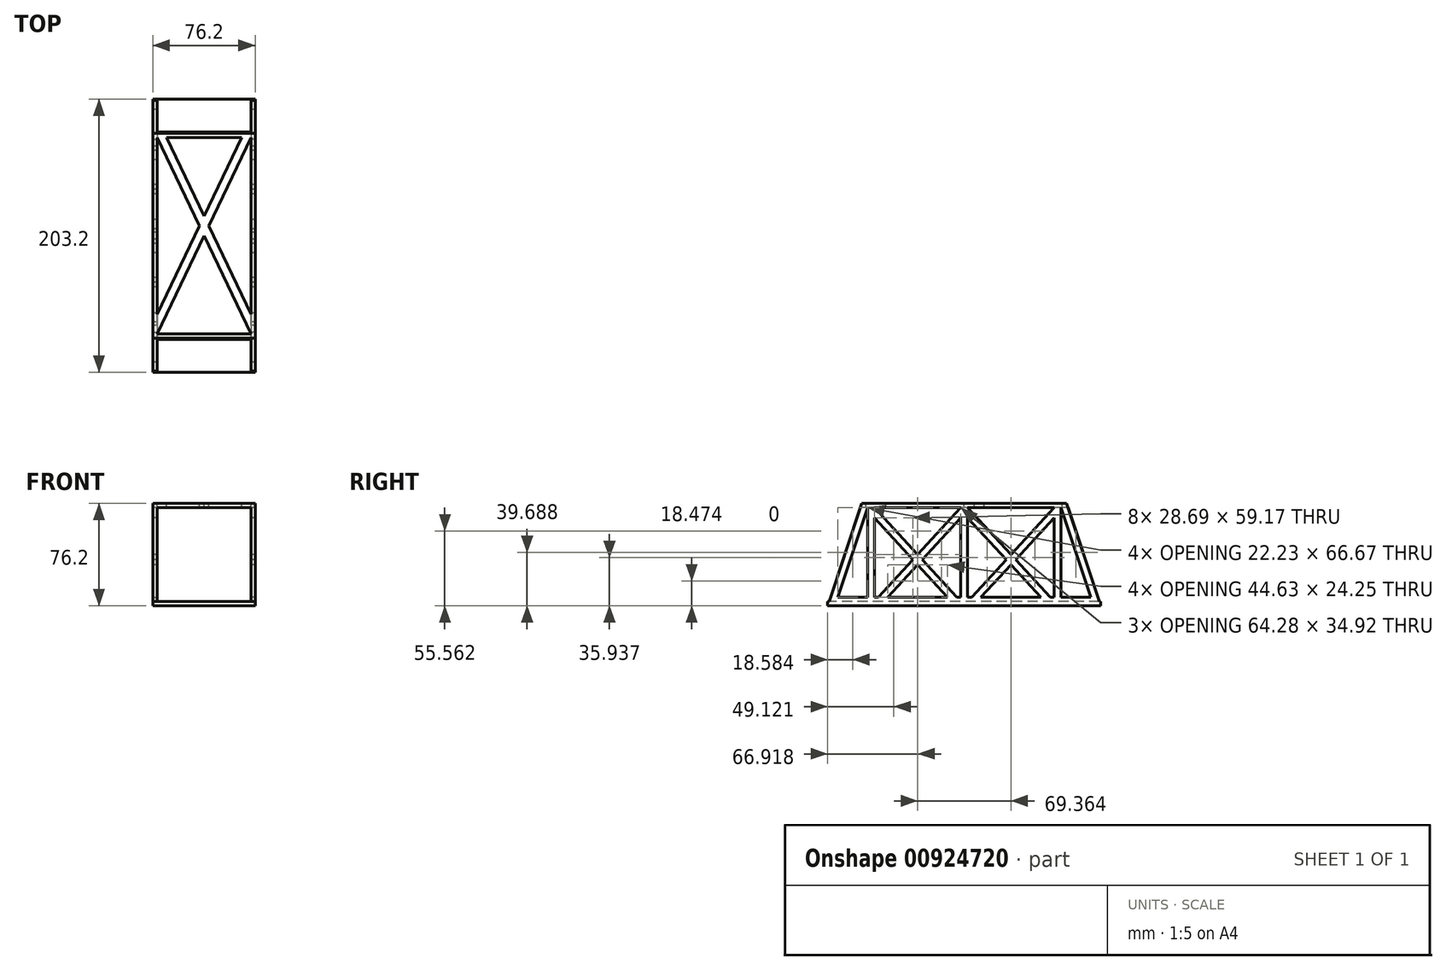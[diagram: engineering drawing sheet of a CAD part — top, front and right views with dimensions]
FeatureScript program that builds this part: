
annotation { "Feature Type Name" : "Feature", "Feature Type Description" : "" }
export const myFeature = defineFeature(function(context is Context, id is Id, definition is map)
    precondition{}
    {
        {
            var Q0;
            Q0=qCreatedBy(makeId("Right.planeOp"),FACE);
            var sketch = newSketch(context, id + "F0", { "sketchPlane" : qUnion([Q0])});
            skLineSegment(sketch, "E0", {"start": v(-101.6, -38.1) * mm, "end": v(101.6, -38.1) * mm});
            skLineSegment(sketch, "E1", {"start": v(101.6, -38.1) * mm, "end": v(76.2, 38.1) * mm});
            skLineSegment(sketch, "E2", {"start": v(76.2, 38.1) * mm, "end": v(-76.2, 38.1) * mm});
            skLineSegment(sketch, "E3", {"start": v(-76.2, 38.1) * mm, "end": v(-101.6, -38.1) * mm});
            skSolve(sketch);
        }
        {
            var Q0;
            Q0=qSketchRegion(id+"F0",true);
            extrude(context, id + "F1", {"entities" : qUnion([Q0]), "endBound" : BoundingType.SYMMETRIC, "depth" : 76.2 * mm, "offsetDistance" : 25.4 * mm});
        }
        {
            var Q0;
            Q0=qCreatedBy(makeId("Front.planeOp"),FACE);
            var sketch = newSketch(context, id + "F2", { "sketchPlane" : qUnion([Q0])});
            skLineSegment(sketch, "E4.bottom", {"start": v(34.92, -34.93) * mm, "end": v(-34.93, -34.93) * mm});
            skLineSegment(sketch, "E4.top", {"start": v(34.92, 34.93) * mm, "end": v(-34.93, 34.92) * mm});
            skLineSegment(sketch, "E4.left", {"start": v(34.92, -34.93) * mm, "end": v(34.92, 34.92) * mm});
            skLineSegment(sketch, "E4.right", {"start": v(-34.93, -34.93) * mm, "end": v(-34.93, 34.92) * mm});
            skPoint(sketch, "E4.middle", {"position": v(0, 0) * mm});
            skSolve(sketch);
        }
        {
            var Q0;
            Q0=qSketchRegion(id+"F2",true);
            extrude(context, id + "F3", {"entities" : qUnion([Q0]), "operationType" : NewBodyOperationType.REMOVE, "endBound" : BoundingType.SYMMETRIC, "oppositeDirection" : true, "depth" : 254 * mm, "offsetDistance" : 25.4 * mm});
        }
        {
            var Q0;
            Q0=makeQuery(id+"F1.opExtrude","CAP_FACE",FACE,{"disambiguationData":[OSD([sQuery(id+"F0.wireOp",EDGE,"E0"),sQuery(id+"F0.wireOp",EDGE,"E1"),sQuery(id+"F0.wireOp",EDGE,"E2"),sQuery(id+"F0.wireOp",EDGE,"E3")])],"isStart":true});
            var sketch = newSketch(context, id + "F4", { "sketchPlane" : qUnion([Q0])});
            skLineSegment(sketch, "E5", {"start": v(-95.19, -34.93) * mm, "end": v(-71.9, 34.93) * mm});
            skLineSegment(sketch, "E6", {"start": v(-71.9, 34.93) * mm, "end": v(-71.9, -34.92) * mm});
            skLineSegment(sketch, "E7", {"start": v(-71.9, -34.92) * mm, "end": v(-95.19, -34.92) * mm});
            skLineSegment(sketch, "E8.MirrorCS", {"start": v(71.9, 34.93) * mm, "end": v(71.9, -34.92) * mm});
            skLineSegment(sketch, "E9.MirrorCS", {"start": v(71.9, -34.92) * mm, "end": v(95.19, -34.92) * mm});
            skLineSegment(sketch, "E10.MirrorCS", {"start": v(95.19, -34.93) * mm, "end": v(71.9, 34.93) * mm});
            skLineSegment(sketch, "E11", {"start": v(-71.9, 34.93) * mm, "end": v(71.9, 34.93) * mm});
            skLineSegment(sketch, "E12", {"start": v(-71.9, -34.92) * mm, "end": v(71.9, -34.92) * mm});
            skLineSegment(sketch, "E13", {"start": v(-66.82, 34.93) * mm, "end": v(-66.82, -34.93) * mm});
            skLineSegment(sketch, "E14", {"start": v(66.82, 34.93) * mm, "end": v(66.82, -34.92) * mm});
            skLineSegment(sketch, "E15.bottom", {"start": v(2.54, -34.93) * mm, "end": v(-2.54, -34.93) * mm});
            skLineSegment(sketch, "E15.top", {"start": v(2.54, 34.93) * mm, "end": v(-2.54, 34.93) * mm});
            skLineSegment(sketch, "E15.left", {"start": v(2.54, -34.93) * mm, "end": v(2.54, 34.93) * mm});
            skLineSegment(sketch, "E15.right", {"start": v(-2.54, -34.93) * mm, "end": v(-2.54, 34.93) * mm});
            skPoint(sketch, "E15.middle", {"position": v(0, 0) * mm});
            skLineSegment(sketch, "E16", {"start": v(-66.82, 34.93) * mm, "end": v(-2.54, -34.93) * mm});
            skLineSegment(sketch, "E17", {"start": v(66.82, 34.93) * mm, "end": v(2.54, -34.93) * mm});
            skLineSegment(sketch, "E18", {"start": v(-66.82, 27.42) * mm, "end": v(-9.44, -34.93) * mm});
            skLineSegment(sketch, "E19", {"start": v(66.82, 27.42) * mm, "end": v(9.44, -34.93) * mm});
            skLineSegment(sketch, "E20", {"start": v(-2.54, 34.93) * mm, "end": v(-66.82, -34.93) * mm});
            skLineSegment(sketch, "E21", {"start": v(-2.54, 27.42) * mm, "end": v(-59.92, -34.93) * mm});
            skLineSegment(sketch, "E22.MirrorCS", {"start": v(2.54, 34.93) * mm, "end": v(66.82, -34.93) * mm});
            skLineSegment(sketch, "E23.MirrorCS", {"start": v(2.54, 27.42) * mm, "end": v(59.92, -34.93) * mm});
            skSolve(sketch);
        }
        {
            var Q0;
            Q0=makeQuery(id+"F4.imprint","IMPRINT",FACE,{"disambiguationData":[TD([[makeQuery(id+"F4.imprint","IMPRINT",EDGE,{"derivedFrom":sQuery(id+"F4.wireOp",EDGE,"E5")}),-1.0]])]});
            var Q1;
            {var subQ1=sQuery(id+"F4.wireOp",EDGE,"E13");var subQ3=sQuery(id+"F4.wireOp",EDGE,"E18");var subQ4=makeQuery(id+"F4.imprint","INTERSECT",VERTEX,{"derivedFrom":[subQ1,subQ3]});Q1=makeQuery(id+"F4.imprint","IMPRINT",FACE,{"disambiguationData":[TD([[makeQuery(id+"F4.imprint","IMPRINT",EDGE,{"disambiguationData":[TD([[subQ4,-1.0]])],"derivedFrom":subQ3}),-1.0]])]});}
            var Q2;
            {var subQ0=sQuery(id+"F4.wireOp",EDGE,"E16");var subQ3=sQuery(id+"F4.wireOp",EDGE,"E20");var subQ5=makeQuery(id+"F4.imprint","INTERSECT",VERTEX,{"derivedFrom":[subQ0,subQ3]});Q2=makeQuery(id+"F4.imprint","IMPRINT",FACE,{"disambiguationData":[TD([[makeQuery(id+"F4.imprint","IMPRINT",EDGE,{"disambiguationData":[TD([[subQ5,1.0]])],"derivedFrom":subQ0}),1.0]])]});}
            var Q3;
            {var subQ1=sQuery(id+"F4.wireOp",EDGE,"E15.right");var subQ3=sQuery(id+"F4.wireOp",EDGE,"E21");var subQ4=makeQuery(id+"F4.imprint","INTERSECT",VERTEX,{"derivedFrom":[subQ1,subQ3]});Q3=makeQuery(id+"F4.imprint","IMPRINT",FACE,{"disambiguationData":[TD([[makeQuery(id+"F4.imprint","IMPRINT",EDGE,{"disambiguationData":[TD([[subQ4,-1.0]])],"derivedFrom":subQ3}),1.0]])]});}
            var Q4;
            {var subQ0=sQuery(id+"F4.wireOp",EDGE,"E18");var subQ1=sQuery(id+"F4.wireOp",EDGE,"E12");var subQ2=makeQuery(id+"F4.imprint","INTERSECT",VERTEX,{"derivedFrom":[subQ1,subQ0]});Q4=makeQuery(id+"F4.imprint","IMPRINT",FACE,{"disambiguationData":[TD([[makeQuery(id+"F4.imprint","IMPRINT",EDGE,{"disambiguationData":[TD([[subQ2,1.0]])],"derivedFrom":subQ1}),1.0]])]});}
            var Q5;
            {var subQ1=sQuery(id+"F4.wireOp",EDGE,"E15.left");var subQ3=sQuery(id+"F4.wireOp",EDGE,"E23.MirrorCS");var subQ4=makeQuery(id+"F4.imprint","INTERSECT",VERTEX,{"derivedFrom":[subQ1,subQ3]});Q5=makeQuery(id+"F4.imprint","IMPRINT",FACE,{"disambiguationData":[TD([[makeQuery(id+"F4.imprint","IMPRINT",EDGE,{"disambiguationData":[TD([[subQ4,-1.0]])],"derivedFrom":subQ3}),-1.0]])]});}
            var Q6;
            {var subQ0=sQuery(id+"F4.wireOp",EDGE,"E17");var subQ3=sQuery(id+"F4.wireOp",EDGE,"E22.MirrorCS");var subQ5=makeQuery(id+"F4.imprint","INTERSECT",VERTEX,{"derivedFrom":[subQ0,subQ3]});Q6=makeQuery(id+"F4.imprint","IMPRINT",FACE,{"disambiguationData":[TD([[makeQuery(id+"F4.imprint","IMPRINT",EDGE,{"disambiguationData":[TD([[subQ5,1.0]])],"derivedFrom":subQ0}),-1.0]])]});}
            var Q7;
            {var subQ1=sQuery(id+"F4.wireOp",EDGE,"E14");var subQ3=sQuery(id+"F4.wireOp",EDGE,"E19");var subQ4=makeQuery(id+"F4.imprint","INTERSECT",VERTEX,{"derivedFrom":[subQ1,subQ3]});Q7=makeQuery(id+"F4.imprint","IMPRINT",FACE,{"disambiguationData":[TD([[makeQuery(id+"F4.imprint","IMPRINT",EDGE,{"disambiguationData":[TD([[subQ4,-1.0]])],"derivedFrom":subQ3}),1.0]])]});}
            var Q8;
            {var subQ0=sQuery(id+"F4.wireOp",EDGE,"E19");var subQ1=sQuery(id+"F4.wireOp",EDGE,"E12");var subQ2=makeQuery(id+"F4.imprint","INTERSECT",VERTEX,{"derivedFrom":[subQ1,subQ0]});Q8=makeQuery(id+"F4.imprint","IMPRINT",FACE,{"disambiguationData":[TD([[makeQuery(id+"F4.imprint","IMPRINT",EDGE,{"disambiguationData":[TD([[subQ2,-1.0]])],"derivedFrom":subQ1}),1.0]])]});}
            var Q9;
            Q9=makeQuery(id+"F4.imprint","IMPRINT",FACE,{"disambiguationData":[TD([[makeQuery(id+"F4.imprint","IMPRINT",EDGE,{"derivedFrom":sQuery(id+"F4.wireOp",EDGE,"E8.MirrorCS")}),1.0]])]});
            extrude(context, id + "F5", {"entities" : qUnion([Q0, Q1, Q2, Q3, Q4, Q5, Q6, Q7, Q8, Q9]), "operationType" : NewBodyOperationType.REMOVE, "oppositeDirection" : true, "depth" : 76.2 * mm, "offsetDistance" : 25.4 * mm});
        }
        {
            var Q0;
            Q0=makeQuery(id+"F1.opExtrude","SWEPT_FACE",FACE,{"disambiguationData":[OSD([sQuery(id+"F0.wireOp",EDGE,"E2")])]});
            var sketch = newSketch(context, id + "F6", { "sketchPlane" : qUnion([Q0])});
            skLineSegment(sketch, "E24.bottom", {"start": v(34.92, -73.03) * mm, "end": v(-34.93, -73.03) * mm});
            skLineSegment(sketch, "E24.top", {"start": v(34.92, 73.03) * mm, "end": v(-34.92, 73.03) * mm});
            skLineSegment(sketch, "E24.left", {"start": v(34.92, -73.03) * mm, "end": v(34.93, 73.02) * mm});
            skLineSegment(sketch, "E24.right", {"start": v(-34.93, -73.03) * mm, "end": v(-34.92, 73.02) * mm});
            skPoint(sketch, "E24.middle", {"position": v(0, 0) * mm});
            skLineSegment(sketch, "E25", {"start": v(-34.92, 73.03) * mm, "end": v(34.92, -73.03) * mm});
            skLineSegment(sketch, "E26", {"start": v(34.92, 73.03) * mm, "end": v(-34.92, -73.03) * mm});
            skLineSegment(sketch, "E27", {"start": v(27.89, 73.03) * mm, "end": v(-34.93, -58.3) * mm});
            skLineSegment(sketch, "E28", {"start": v(-27.89, 73.02) * mm, "end": v(34.93, -58.3) * mm});
            skSolve(sketch);
        }
        {
            var Q0;
            {var subQ1=sQuery(id+"F6.wireOp",EDGE,"E24.right");var subQ3=sQuery(id+"F6.wireOp",EDGE,"E27");var subQ4=makeQuery(id+"F6.imprint","INTERSECT",VERTEX,{"derivedFrom":[subQ1,subQ3]});Q0=makeQuery(id+"F6.imprint","IMPRINT",FACE,{"disambiguationData":[TD([[makeQuery(id+"F6.imprint","IMPRINT",EDGE,{"disambiguationData":[TD([[subQ4,1.0]])],"derivedFrom":subQ3}),-1.0]])]});}
            var Q1;
            {var subQ0=sQuery(id+"F6.wireOp",EDGE,"E24.bottom");Q1=makeQuery(id+"F6.imprint","IMPRINT",FACE,{"disambiguationData":[TD([[makeQuery(id+"F6.imprint","IMPRINT",EDGE,{"derivedFrom":subQ0}),-1.0]])]});}
            var Q2;
            {var subQ1=sQuery(id+"F6.wireOp",EDGE,"E24.left");var subQ3=sQuery(id+"F6.wireOp",EDGE,"E28");var subQ4=makeQuery(id+"F6.imprint","INTERSECT",VERTEX,{"derivedFrom":[subQ1,subQ3]});Q2=makeQuery(id+"F6.imprint","IMPRINT",FACE,{"disambiguationData":[TD([[makeQuery(id+"F6.imprint","IMPRINT",EDGE,{"disambiguationData":[TD([[subQ4,1.0]])],"derivedFrom":subQ3}),1.0]])]});}
            var Q3;
            {var subQ0=sQuery(id+"F6.wireOp",EDGE,"E27");var subQ1=sQuery(id+"F6.wireOp",EDGE,"E24.top");var subQ2=makeQuery(id+"F6.imprint","INTERSECT",VERTEX,{"derivedFrom":[subQ1,subQ0]});Q3=makeQuery(id+"F6.imprint","IMPRINT",FACE,{"disambiguationData":[TD([[makeQuery(id+"F6.imprint","IMPRINT",EDGE,{"disambiguationData":[TD([[subQ2,-1.0]])],"derivedFrom":subQ1}),1.0]])]});}
            extrude(context, id + "F7", {"entities" : qUnion([Q0, Q1, Q2, Q3]), "operationType" : NewBodyOperationType.REMOVE, "oppositeDirection" : true, "depth" : 25.4 * mm, "offsetDistance" : 25.4 * mm});
        }
        {
            var Q0;
            {var subQ0=sQuery(id+"F4.wireOp",EDGE,"E12");Q0=makeQuery(id+"F5.boolean.opBoolean","MERGE",FACE,{"derivedFrom":[makeQuery(id+"F3.boolean.opBoolean","COPY",FACE,{"derivedFrom":makeQuery(id+"F3.opExtrude","SWEPT_FACE",FACE,{"disambiguationData":[OSD([sQuery(id+"F2.wireOp",EDGE,"E4.bottom")])]})})],"fromTools":[makeQuery(id+"F5.opExtrude","SWEPT_FACE",FACE,{"disambiguationData":[OSD([sQuery(id+"F4.wireOp",EDGE,"E7")])]}),makeQuery(id+"F5.opExtrude","SWEPT_FACE",FACE,{"disambiguationData":[OSD([sQuery(id+"F4.wireOp",EDGE,"E9.MirrorCS")])]}),makeQuery(id+"F5.opExtrude","SWEPT_FACE",FACE,{"disambiguationData":[OSD([subQ0]),TDD([makeQuery(id+"F4.imprint","IMPRINT",EDGE,{"disambiguationData":[TD([[makeQuery(id+"F4.imprint","INTERSECT",VERTEX,{"derivedFrom":[subQ0,sQuery(id+"F4.wireOp",EDGE,"E18")]}),1.0]])],"derivedFrom":subQ0})])]}),makeQuery(id+"F5.opExtrude","SWEPT_FACE",FACE,{"disambiguationData":[OSD([subQ0]),TDD([makeQuery(id+"F4.imprint","IMPRINT",EDGE,{"disambiguationData":[TD([[makeQuery(id+"F4.imprint","INTERSECT",VERTEX,{"derivedFrom":[subQ0,sQuery(id+"F4.wireOp",EDGE,"E19")]}),-1.0]])],"derivedFrom":subQ0})])]})]});}
            var sketch = newSketch(context, id + "F8", { "sketchPlane" : qUnion([Q0])});
            skLineSegment(sketch, "E29.bottom", {"start": v(-38.1, -95.19) * mm, "end": v(-34.93, -95.19) * mm});
            skLineSegment(sketch, "E29.top", {"start": v(-38.1, 95.19) * mm, "end": v(-34.93, 95.19) * mm});
            skLineSegment(sketch, "E29.left", {"start": v(-38.1, -95.19) * mm, "end": v(-38.1, 95.19) * mm});
            skLineSegment(sketch, "E29.right", {"start": v(-34.93, -95.19) * mm, "end": v(-34.93, 95.19) * mm});
            skLineSegment(sketch, "E30.MirrorCS", {"start": v(38.1, -95.19) * mm, "end": v(34.93, -95.19) * mm});
            skLineSegment(sketch, "E31.MirrorCS", {"start": v(38.1, -95.19) * mm, "end": v(38.1, 95.19) * mm});
            skLineSegment(sketch, "E32.MirrorCS", {"start": v(34.93, -95.19) * mm, "end": v(34.93, 95.19) * mm});
            skLineSegment(sketch, "E33.MirrorCS", {"start": v(38.1, 95.19) * mm, "end": v(34.93, 95.19) * mm});
            skSolve(sketch);
        }
        {
            var Q0;
            Q0=qSketchRegion(id+"F8",true);
            extrude(context, id + "F9", {"entities" : qUnion([Q0]), "operationType" : NewBodyOperationType.ADD, "depth" : 3.17 * mm, "offsetDistance" : 25.4 * mm});
        }
        {
            var Q0;
            Q0=makeQuery(id+"F9.boolean.opBoolean","MERGE",FACE,{"derivedFrom":[makeQuery(id+"F1.opExtrude","CAP_FACE",FACE,{"disambiguationData":[OSD([sQuery(id+"F0.wireOp",EDGE,"E0"),sQuery(id+"F0.wireOp",EDGE,"E1"),sQuery(id+"F0.wireOp",EDGE,"E2"),sQuery(id+"F0.wireOp",EDGE,"E3")])],"isStart":false}),makeQuery(id+"F9.opExtrude","SWEPT_FACE",FACE,{"disambiguationData":[OSD([sQuery(id+"F8.wireOp",EDGE,"E31.MirrorCS")])]})]});
            var sketch = newSketch(context, id + "F10", { "sketchPlane" : qUnion([Q0])});
            skLineSegment(sketch, "E34.bottom", {"start": v(-101.6, -38.1) * mm, "end": v(-97.33, -38.1) * mm});
            skLineSegment(sketch, "E34.top", {"start": v(-101.6, -34.93) * mm, "end": v(-97.33, -34.93) * mm});
            skLineSegment(sketch, "E34.left", {"start": v(-101.6, -38.1) * mm, "end": v(-101.6, -34.93) * mm});
            skLineSegment(sketch, "E34.right", {"start": v(-97.33, -38.1) * mm, "end": v(-97.33, -34.93) * mm});
            skLineSegment(sketch, "E35.MirrorCS", {"start": v(97.33, -38.1) * mm, "end": v(97.33, -34.93) * mm});
            skLineSegment(sketch, "E36.MirrorCS", {"start": v(101.6, -34.93) * mm, "end": v(97.33, -34.93) * mm});
            skLineSegment(sketch, "E37.MirrorCS", {"start": v(101.6, -38.1) * mm, "end": v(101.6, -34.93) * mm});
            skLineSegment(sketch, "E38.MirrorCS", {"start": v(101.6, -38.1) * mm, "end": v(97.33, -38.1) * mm});
            skSolve(sketch);
        }
        {
            var Q0;
            Q0=qSketchRegion(id+"F10",true);
            extrude(context, id + "F11", {"entities" : qUnion([Q0]), "operationType" : NewBodyOperationType.ADD, "oppositeDirection" : true, "depth" : 76.2 * mm, "offsetDistance" : 25.4 * mm});
        }
    });
